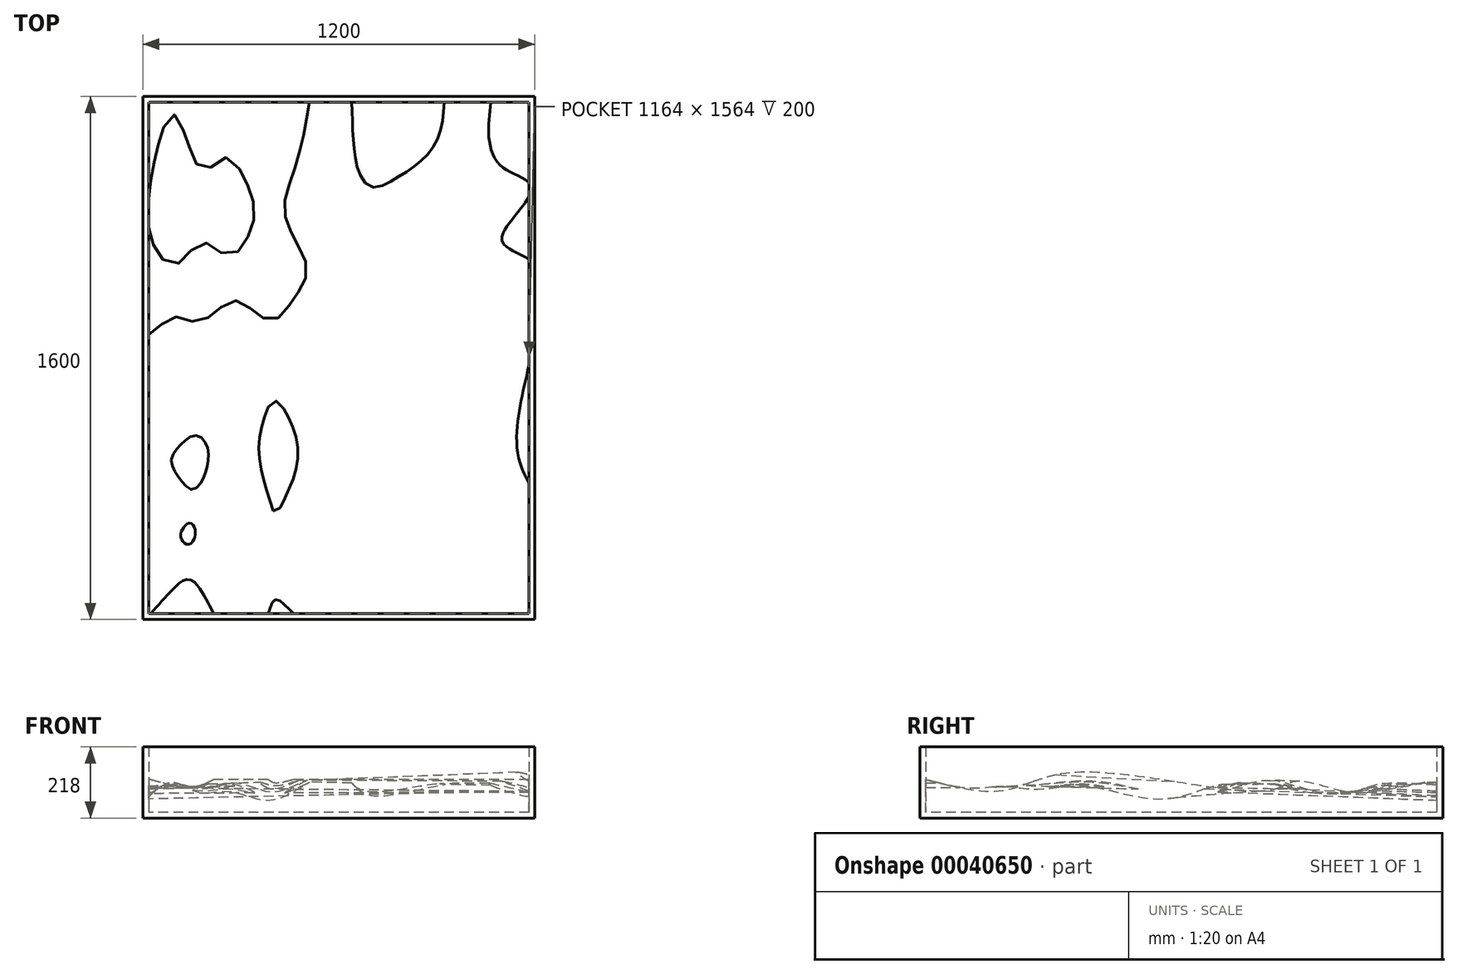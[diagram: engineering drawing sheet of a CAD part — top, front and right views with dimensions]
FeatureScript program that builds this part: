
annotation { "Feature Type Name" : "Feature", "Feature Type Description" : "" }
export const myFeature = defineFeature(function(context is Context, id is Id, definition is map)
    precondition{}
    {
        {
            var Q0;
            Q0=qCreatedBy(makeId("Top.planeOp"),FACE);
            var sketch = newSketch(context, id + "F0", { "sketchPlane" : qUnion([Q0])});
            skLineSegment(sketch, "E0.rect.bottom", {"start": v(600, 800) * mm, "end": v(-600, 800) * mm});
            skLineSegment(sketch, "E0.rect.top", {"start": v(600, -800) * mm, "end": v(-600, -800) * mm});
            skLineSegment(sketch, "E0.rect.left", {"start": v(600, 800) * mm, "end": v(600, -800) * mm});
            skLineSegment(sketch, "E0.rect.right", {"start": v(-600, 800) * mm, "end": v(-600, -800) * mm});
            skPoint(sketch, "E0.rect.middle", {"position": v(0, 0) * mm});
            skSolve(sketch);
        }
        {
            var Q0;
            Q0=makeQuery(id+"F0.imprint","IMPRINT",FACE,{"disambiguationData":[TD([[makeQuery(id+"F0.imprint","IMPRINT",EDGE,{"derivedFrom":sQuery(id+"F0.wireOp",EDGE,"E0.rect.bottom")}),1.0]])]});
            extrude(context, id + "F1", {"entities" : qUnion([Q0]), "depth" : 18 * mm});
        }
        {
            var Q0;
            Q0=makeQuery(id+"F1.opExtrude","CAP_FACE",FACE,{"disambiguationData":[OSD([sQuery(id+"F0.wireOp",EDGE,"E0.rect.bottom"),sQuery(id+"F0.wireOp",EDGE,"E0.rect.top"),sQuery(id+"F0.wireOp",EDGE,"E0.rect.left"),sQuery(id+"F0.wireOp",EDGE,"E0.rect.right")])],"isStart":false});
            var sketch = newSketch(context, id + "F2", { "sketchPlane" : qUnion([Q0])});
            skLineSegment(sketch, "E1.rect.bottom", {"start": v(600, 800) * mm, "end": v(-600, 800) * mm});
            skLineSegment(sketch, "E1.rect.top", {"start": v(600, -800) * mm, "end": v(-600, -800) * mm});
            skLineSegment(sketch, "E1.rect.left", {"start": v(600, 800) * mm, "end": v(600, -800) * mm});
            skLineSegment(sketch, "E1.rect.right", {"start": v(-600, 800) * mm, "end": v(-600, -800) * mm});
            skPoint(sketch, "E1.rect.middle", {"position": v(0, 0) * mm});
            skPoint(sketch, "E2.rect.middle", {"position": v(0, 1.19) * mm});
            skLineSegment(sketch, "E3.0", {"start": v(582, 782) * mm, "end": v(582, -782) * mm});
            skLineSegment(sketch, "E3.1", {"start": v(582, 782) * mm, "end": v(-582, 782) * mm});
            skLineSegment(sketch, "E3.2", {"start": v(-582, 782) * mm, "end": v(-582, -782) * mm});
            skLineSegment(sketch, "E3.3", {"start": v(582, -782) * mm, "end": v(-582, -782) * mm});
            skSolve(sketch);
        }
        {
            var Q0;
            Q0=makeQuery(id+"F2.imprint","IMPRINT",FACE,{"disambiguationData":[TD([[makeQuery(id+"F2.imprint","IMPRINT",EDGE,{"derivedFrom":sQuery(id+"F2.wireOp",EDGE,"E1.rect.bottom")}),1.0]])]});
            extrude(context, id + "F3", {"entities" : qUnion([Q0]), "operationType" : NewBodyOperationType.ADD, "depth" : 200 * mm});
        }
        {
            var Q0;
            Q0=makeQuery(id+"F3.opExtrude","SWEPT_FACE",FACE,{"disambiguationData":[OSD([sQuery(id+"F2.wireOp",EDGE,"E3.1")])]});
            var sketch = newSketch(context, id + "F4", { "sketchPlane" : qUnion([Q0])});
            skFitSpline(sketch, "E4", {"points": [v(-582, 64.93) * mm, v(-507.47, 109.64) * mm, v(-432.33, 79.41) * mm, v(-335.32, 81.45) * mm, v(-215.1, 54.68) * mm, v(-89.4, 110.1) * mm, v(0, 137.67) * mm, v(54.06, 92.76) * mm, v(129.2, 68) * mm, v(397.2, 111.85) * mm, v(496.23, 88.47) * mm, v(582, 65.26) * mm], "startDerivative": vector(909.8, 835.65) * mm, "endDerivative": vector(1070.58, -245.02) * mm});
            skSolve(sketch);
        }
        {
            var Q0;
            {var subQ2=sQuery(id+"F4.wireOp",EDGE,"E4");Q0=makeQuery(id+"F4.imprint","IMPRINT",FACE,{"disambiguationData":[TD([[makeQuery(id+"F4.imprint","IMPRINT",EDGE,{"derivedFrom":subQ2}),1.0]])]});}
            cPlane(context, id + "F5", {"entities" : qUnion([Q0]), "cplaneType" : CPlaneType.OFFSET, "offset" : 1564 * mm, "width" : 150 * mm, "height" : 150 * mm});
        }
        {
            var Q0;
            Q0=qCreatedBy(id+"F5.planeOp",FACE);
            var sketch = newSketch(context, id + "F6", { "sketchPlane" : qUnion([Q0])});
            skFitSpline(sketch, "E5", {"points": [v(-582, 119.56) * mm, v(-433.47, 96.99) * mm, v(-296.3, 151.33) * mm, v(-215.52, 117.74) * mm, v(-185.5, 108.3) * mm, v(-48.31, 137.35) * mm, v(0, 132.17) * mm, v(97.16, 150.2) * mm, v(312.9, 186.05) * mm, v(582, 155.81) * mm], "startDerivative": vector(1487.6, -363.08) * mm, "endDerivative": vector(2107.62, -984.72) * mm});
            skLineSegment(sketch, "E6", {"start": v(-582, 119.56) * mm, "end": v(-582, 0) * mm});
            skLineSegment(sketch, "E7", {"start": v(-582, 0) * mm, "end": v(582, 0) * mm});
            skLineSegment(sketch, "E8", {"start": v(582, 0) * mm, "end": v(582, 155.81) * mm});
            skSolve(sketch);
        }
        {
            var Q0;
            Q0=makeQuery(id+"F6.imprint","IMPRINT",FACE,{"disambiguationData":[TD([[makeQuery(id+"F6.imprint","IMPRINT",EDGE,{"derivedFrom":sQuery(id+"F6.wireOp",EDGE,"E5")}),-1.0]])]});
            var Q1;
            {var subQ2=sQuery(id+"F4.wireOp",EDGE,"E4");Q1=makeQuery(id+"F4.imprint","IMPRINT",FACE,{"disambiguationData":[TD([[makeQuery(id+"F4.imprint","IMPRINT",EDGE,{"derivedFrom":subQ2}),-1.0]])]});}
            loft(context, id + "F7", {"sheetProfilesArray" : [{ "sheetProfileEntities" : qUnion([Q0]) }, { "sheetProfileEntities" : qUnion([Q1]) }]});
        }
        {
            var Q0;
            Q0=makeQuery(id+"F3.opExtrude","SWEPT_FACE",FACE,{"disambiguationData":[OSD([sQuery(id+"F2.wireOp",EDGE,"E3.2")])]});
            var sketch = newSketch(context, id + "F8", { "sketchPlane" : qUnion([Q0])});
            skPoint(sketch, "E9.6.internal.snap0", {"position": v(-782, 118) * mm});
            skFitSpline(sketch, "E9", {"points": [v(-782, 118) * mm, v(-647.05, 92.05) * mm, v(-548.57, 97.23) * mm, v(-441.4, 88.82) * mm, v(-287.3, 97.4) * mm, v(-47.07, 59.16) * mm, v(172.67, 118) * mm, v(359.49, 83.83) * mm, v(616.36, 85.48) * mm, v(782, 118) * mm], "startDerivative": vector(1412.5, -371.84) * mm, "endDerivative": vector(1387.97, 325.16) * mm});
            skSolve(sketch);
        }
        {
            var Q0;
            Q0=makeQuery(id+"F3.opExtrude","SWEPT_FACE",FACE,{"disambiguationData":[OSD([sQuery(id+"F2.wireOp",EDGE,"E3.0")])]});
            var sketch = newSketch(context, id + "F9", { "sketchPlane" : qUnion([Q0])});
            skFitSpline(sketch, "E10", {"points": [v(-782, 98.42) * mm, v(-592.32, 102.2) * mm, v(-523.5, 78.12) * mm, v(-373.32, 112.14) * mm, v(-253.2, 82.78) * mm, v(317.37, 141.33) * mm, v(547.06, 83.55) * mm, v(782, 118) * mm], "startDerivative": vector(1607.66, 181.2) * mm, "endDerivative": vector(1622.8, 435) * mm});
            skSolve(sketch);
        }
        {
            var Q1;
            {var subQ2=sQuery(id+"F9.wireOp",EDGE,"E10");Q1=makeQuery(id+"F9.imprint","IMPRINT",FACE,{"disambiguationData":[TD([[makeQuery(id+"F9.imprint","IMPRINT",EDGE,{"derivedFrom":subQ2}),-1.0]])]});}
            var Q2;
            {var subQ2=sQuery(id+"F8.wireOp",EDGE,"E9");Q2=makeQuery(id+"F8.imprint","IMPRINT",FACE,{"disambiguationData":[TD([[makeQuery(id+"F8.imprint","IMPRINT",EDGE,{"derivedFrom":subQ2}),-1.0]])]});}
            loft(context, id + "F10", {"sheetProfilesArray" : [{ "sheetProfileEntities" : qUnion([Q1]) }, { "sheetProfileEntities" : qUnion([Q2]) }]});
        }
        {
            var Q0;
            {var subQ2=sQuery(id+"F4.wireOp",EDGE,"E4");Q0=makeQuery(id+"F7.opLoft","SWEPT_BODY",BODY,{"disambiguationData":[OSD([makeQuery(id+"F4.imprint","IMPRINT",FACE,{"disambiguationData":[TD([[makeQuery(id+"F4.imprint","IMPRINT",EDGE,{"derivedFrom":subQ2}),-1.0]])]}),makeQuery(id+"F6.imprint","IMPRINT",FACE,{"disambiguationData":[TD([[makeQuery(id+"F6.imprint","IMPRINT",EDGE,{"derivedFrom":sQuery(id+"F6.wireOp",EDGE,"E5")}),-1.0]])]})])]});}
            var Q1;
            {var subQ3=sQuery(id+"F8.wireOp",EDGE,"E9");var subQ9=sQuery(id+"F9.wireOp",EDGE,"E10");Q1=makeQuery(id+"F10.opLoft","SWEPT_BODY",BODY,{"disambiguationData":[OSD([makeQuery(id+"F8.imprint","IMPRINT",FACE,{"disambiguationData":[TD([[makeQuery(id+"F8.imprint","IMPRINT",EDGE,{"derivedFrom":subQ3}),-1.0]])]}),makeQuery(id+"F9.imprint","IMPRINT",FACE,{"disambiguationData":[TD([[makeQuery(id+"F9.imprint","IMPRINT",EDGE,{"derivedFrom":subQ9}),-1.0]])]})])]});}
            booleanBodies(context, id + "F11", {"operationType" : BooleanOperationType.INTERSECTION, "tools" : qUnion([Q0, Q1])});
        }
    });
